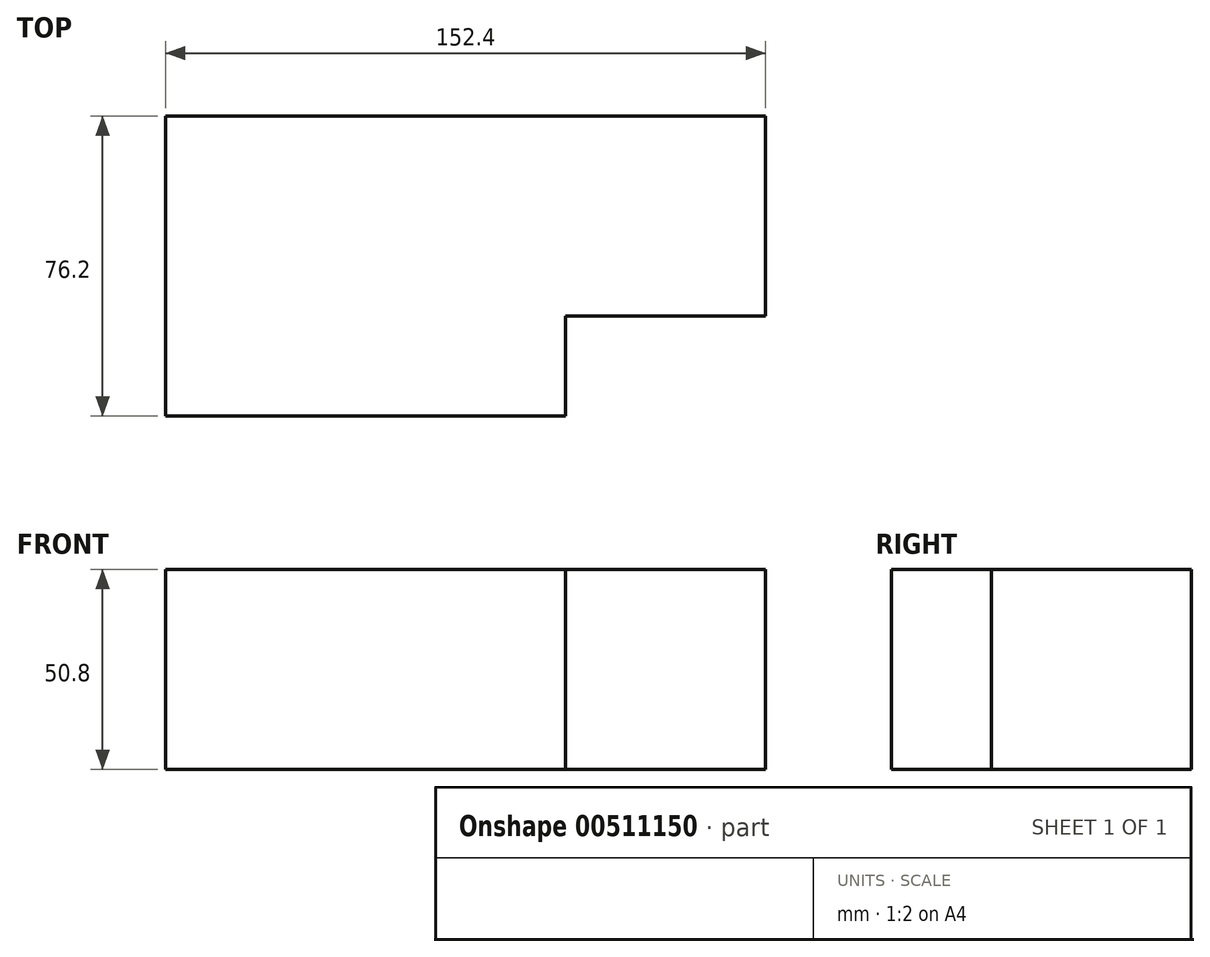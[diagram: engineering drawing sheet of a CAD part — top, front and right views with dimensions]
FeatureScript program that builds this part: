
annotation { "Feature Type Name" : "Feature", "Feature Type Description" : "" }
export const myFeature = defineFeature(function(context is Context, id is Id, definition is map)
    precondition{}
    {
        {
            var Q0;
            Q0=qCreatedBy(makeId("Top.planeOp"),FACE);
            var sketch = newSketch(context, id + "F0", { "sketchPlane" : qUnion([Q0])});
            skLineSegment(sketch, "E0.bottom", {"start": v(-46.83, 42.67) * mm, "end": v(105.57, 42.67) * mm});
            skLineSegment(sketch, "E0.top", {"start": v(-46.83, -33.53) * mm, "end": v(105.57, -33.53) * mm});
            skLineSegment(sketch, "E0.left", {"start": v(-46.83, 42.67) * mm, "end": v(-46.83, -33.53) * mm});
            skLineSegment(sketch, "E0.right", {"start": v(105.57, 42.67) * mm, "end": v(105.57, -33.53) * mm});
            skLineSegment(sketch, "E1.bottom", {"start": v(54.77, -8.13) * mm, "end": v(105.57, -8.13) * mm});
            skLineSegment(sketch, "E1.top", {"start": v(54.77, -33.53) * mm, "end": v(105.57, -33.53) * mm});
            skLineSegment(sketch, "E1.left", {"start": v(54.77, -8.13) * mm, "end": v(54.77, -33.53) * mm});
            skLineSegment(sketch, "E1.right", {"start": v(105.57, -8.13) * mm, "end": v(105.57, -33.53) * mm});
            skSolve(sketch);
        }
        {
            var Q0;
            Q0=makeQuery(id+"F0.imprint","IMPRINT",FACE,{"disambiguationData":[TD([[makeQuery(id+"F0.imprint","IMPRINT",EDGE,{"derivedFrom":sQuery(id+"F0.wireOp",EDGE,"E0.bottom")}),-1.0]])]});
            extrude(context, id + "F1", {"entities" : qUnion([Q0]), "depth" : 50.8 * mm});
        }
    });
